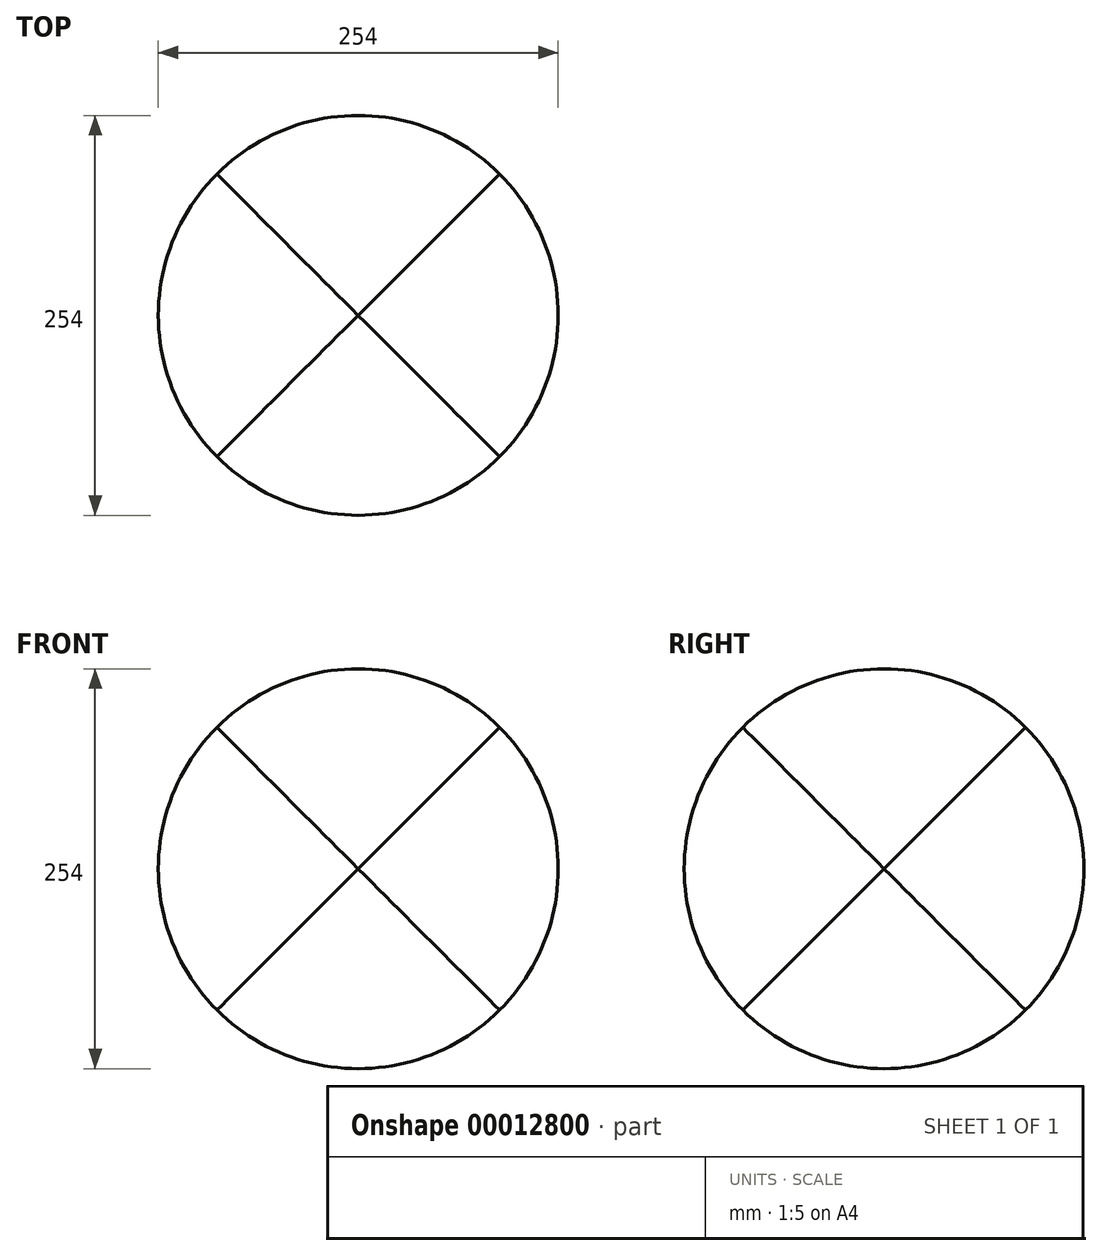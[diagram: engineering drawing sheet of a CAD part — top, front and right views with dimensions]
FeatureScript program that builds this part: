
annotation { "Feature Type Name" : "Feature", "Feature Type Description" : "" }
export const myFeature = defineFeature(function(context is Context, id is Id, definition is map)
    precondition{}
    {
        {
            var Q0;
            Q0=qCreatedBy(makeId("Top.planeOp"),FACE);
            var sketch = newSketch(context, id + "F0", { "sketchPlane" : qUnion([Q0])});
            skCircle(sketch, "E0", {"center": v(0, 0) * mm, "radius": 127 * mm});
            skLineSegment(sketch, "E1", {"start": v(0, -127) * mm, "end": v(0, 127) * mm, "construction": true});
            skLineSegment(sketch, "E2", {"start": v(-127, 0) * mm, "end": v(127, 0) * mm, "construction": true});
            skSolve(sketch);
        }
        {
            var Q0;
            Q0=makeQuery(id+"F0.imprint","IMPRINT",FACE,{"disambiguationData":[TD([[makeQuery(id+"F0.imprint","IMPRINT",EDGE,{"derivedFrom":sQuery(id+"F0.wireOp",EDGE,"E0")}),1.0]])]});
            extrude(context, id + "F1", {"entities" : qUnion([Q0]), "endBound" : BoundingType.SYMMETRIC, "depth" : 254 * mm});
        }
        {
            var Q0;
            Q0=makeQuery(id+"F1.opExtrude","SWEPT_BODY",BODY,{"disambiguationData":[OSD([sQuery(id+"F0.wireOp",EDGE,"E0")])]});
            var Q1;
            Q1=sQuery(id+"F0.wireOp",EDGE,"E1");
            circularPattern(context, id + "F2", {"entities" : qUnion([Q0]), "axis" : qUnion([Q1]), "angle" : 90 * degree, "instanceCount" : 2});
        }
        {
            var Q0;
            Q0=makeQuery(id+"F1.opExtrude","SWEPT_BODY",BODY,{"disambiguationData":[OSD([sQuery(id+"F0.wireOp",EDGE,"E0")])]});
            var Q1;
            Q1=sQuery(id+"F0.wireOp",EDGE,"E2");
            circularPattern(context, id + "F3", {"entities" : qUnion([Q0]), "axis" : qUnion([Q1]), "angle" : 90 * degree, "instanceCount" : 2});
        }
        {
            var Q0;
            Q0=makeQuery(id+"F1.opExtrude","SWEPT_BODY",BODY,{"disambiguationData":[OSD([sQuery(id+"F0.wireOp",EDGE,"E0")])]});
            var Q1;
            Q1=makeQuery(id+"F2.opPattern","COPY",BODY,{"derivedFrom":makeQuery(id+"F1.opExtrude","SWEPT_BODY",BODY,{"disambiguationData":[OSD([sQuery(id+"F0.wireOp",EDGE,"E0")])]}),"instanceName":"1"});
            var Q2;
            Q2=makeQuery(id+"F3.opPattern","COPY",BODY,{"derivedFrom":makeQuery(id+"F1.opExtrude","SWEPT_BODY",BODY,{"disambiguationData":[OSD([sQuery(id+"F0.wireOp",EDGE,"E0")])]}),"instanceName":"1"});
            booleanBodies(context, id + "F4", {"operationType" : BooleanOperationType.INTERSECTION, "tools" : qUnion([Q0, Q1, Q2])});
        }
    });
